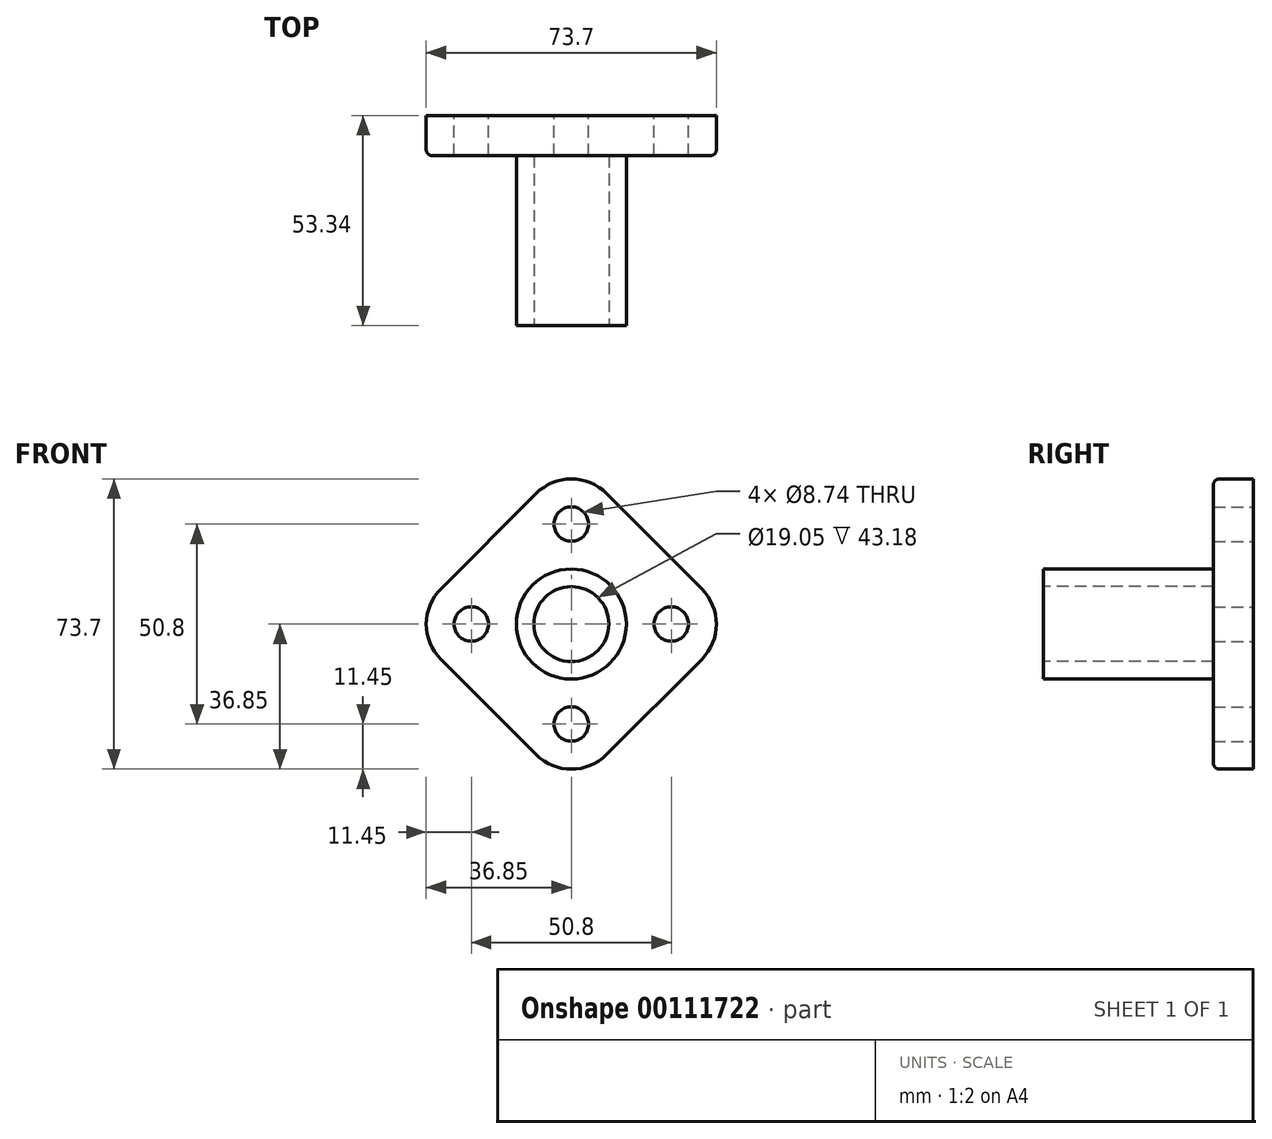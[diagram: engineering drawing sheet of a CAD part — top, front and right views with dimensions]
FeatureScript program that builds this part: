
annotation { "Feature Type Name" : "Feature", "Feature Type Description" : "" }
export const myFeature = defineFeature(function(context is Context, id is Id, definition is map)
    precondition{}
    {
        {
            var Q0;
            Q0=qCreatedBy(makeId("Front.planeOp"),FACE);
            var sketch = newSketch(context, id + "F0", { "sketchPlane" : qUnion([Q0])});
            skLineSegment(sketch, "E0", {"start": v(0, 0) * mm, "end": v(-42.11, 0) * mm});
            skLineSegment(sketch, "E1", {"start": v(0, 0) * mm, "end": v(42.11, 0) * mm});
            skLineSegment(sketch, "E2", {"start": v(0, 0) * mm, "end": v(0, 42.11) * mm});
            skLineSegment(sketch, "E3", {"start": v(0, 0) * mm, "end": v(0, -42.11) * mm});
            skLineSegment(sketch, "E4", {"start": v(0, -42.11) * mm, "end": v(42.11, 0) * mm});
            skLineSegment(sketch, "E5", {"start": v(42.11, 0) * mm, "end": v(0, 42.11) * mm});
            skLineSegment(sketch, "E6", {"start": v(0, 42.11) * mm, "end": v(-42.11, 0) * mm});
            skLineSegment(sketch, "E7", {"start": v(-42.11, 0) * mm, "end": v(0, -42.11) * mm});
            skCircle(sketch, "E8", {"center": v(-25.4, 0) * mm, "radius": 4.37 * mm});
            skCircle(sketch, "E9", {"center": v(25.4, 0) * mm, "radius": 4.37 * mm});
            skCircle(sketch, "E10", {"center": v(0, 25.4) * mm, "radius": 4.37 * mm});
            skCircle(sketch, "E11", {"center": v(0, -25.4) * mm, "radius": 4.37 * mm});
            skSolve(sketch);
        }
        {
            var Q0;
            {var subQ0=sQuery(id+"F0.wireOp",EDGE,"E5");Q0=makeQuery(id+"F0.imprint","IMPRINT",FACE,{"disambiguationData":[TD([[makeQuery(id+"F0.imprint","IMPRINT",EDGE,{"derivedFrom":subQ0}),1.0]])]});}
            var Q1;
            {var subQ0=sQuery(id+"F0.wireOp",EDGE,"E4");Q1=makeQuery(id+"F0.imprint","IMPRINT",FACE,{"disambiguationData":[TD([[makeQuery(id+"F0.imprint","IMPRINT",EDGE,{"derivedFrom":subQ0}),1.0]])]});}
            var Q2;
            {var subQ0=sQuery(id+"F0.wireOp",EDGE,"E7");Q2=makeQuery(id+"F0.imprint","IMPRINT",FACE,{"disambiguationData":[TD([[makeQuery(id+"F0.imprint","IMPRINT",EDGE,{"derivedFrom":subQ0}),1.0]])]});}
            var Q3;
            {var subQ0=sQuery(id+"F0.wireOp",EDGE,"E6");Q3=makeQuery(id+"F0.imprint","IMPRINT",FACE,{"disambiguationData":[TD([[makeQuery(id+"F0.imprint","IMPRINT",EDGE,{"derivedFrom":subQ0}),1.0]])]});}
            extrude(context, id + "F1", {"entities" : qUnion([Q0, Q1, Q2, Q3]), "depth" : 10.16 * mm});
        }
        {
            var Q0;
            Q0=makeQuery(id+"F1.opExtrude","SWEPT_EDGE",EDGE,{"disambiguationData":[OSD([sQuery(id+"F0.wireOp",EDGE,"E2"),sQuery(id+"F0.wireOp",EDGE,"E5"),sQuery(id+"F0.wireOp",EDGE,"E6")])]});
            var Q1;
            Q1=makeQuery(id+"F1.opExtrude","SWEPT_EDGE",EDGE,{"disambiguationData":[OSD([sQuery(id+"F0.wireOp",EDGE,"E0"),sQuery(id+"F0.wireOp",EDGE,"E6"),sQuery(id+"F0.wireOp",EDGE,"E7")])]});
            fillet(context, id + "F2", {"entities" : qUnion([Q0, Q1]), "radius" : 12.7 * mm, "tangentPropagation" : true, "allowEdgeOverflow" : false});
        }
        {
            var Q0;
            Q0=makeQuery(id+"F1.opExtrude","SWEPT_EDGE",EDGE,{"disambiguationData":[OSD([sQuery(id+"F0.wireOp",EDGE,"E1"),sQuery(id+"F0.wireOp",EDGE,"E4"),sQuery(id+"F0.wireOp",EDGE,"E5")])]});
            var Q1;
            Q1=makeQuery(id+"F1.opExtrude","SWEPT_EDGE",EDGE,{"disambiguationData":[OSD([sQuery(id+"F0.wireOp",EDGE,"E3"),sQuery(id+"F0.wireOp",EDGE,"E4"),sQuery(id+"F0.wireOp",EDGE,"E7")])]});
            fillet(context, id + "F3", {"entities" : qUnion([Q0, Q1]), "radius" : 12.7 * mm, "tangentPropagation" : true, "allowEdgeOverflow" : false});
        }
        {
            var Q0;
            Q0=makeQuery(id+"F1.opExtrude","CAP_EDGE",EDGE,{"disambiguationData":[OSD([sQuery(id+"F0.wireOp",EDGE,"E6")])],"isStart":false});
            var Q1;
            {var subQ0=sQuery(id+"F0.wireOp",EDGE,"E6");var subQ1=sQuery(id+"F0.wireOp",EDGE,"E5");Q1=makeQuery(id+"F2.opFillet","BLEND_EDGE",EDGE,{"blendedFrom":[makeQuery(id+"F1.opExtrude","SWEPT_EDGE",EDGE,{"disambiguationData":[OSD([sQuery(id+"F0.wireOp",EDGE,"E2"),subQ1,subQ0])]}),makeQuery(id+"F1.opExtrude","CAP_FACE",FACE,{"disambiguationData":[OSD([sQuery(id+"F0.wireOp",EDGE,"E4"),subQ1,subQ0,sQuery(id+"F0.wireOp",EDGE,"E7"),sQuery(id+"F0.wireOp",EDGE,"E8"),sQuery(id+"F0.wireOp",EDGE,"E9"),sQuery(id+"F0.wireOp",EDGE,"E10"),sQuery(id+"F0.wireOp",EDGE,"E11")])],"isStart":false})],"blendedInto":[makeQuery(id+"F1.opExtrude","CAP_FACE",FACE,{"disambiguationData":[OSD([sQuery(id+"F0.wireOp",EDGE,"E4"),subQ1,subQ0,sQuery(id+"F0.wireOp",EDGE,"E7"),sQuery(id+"F0.wireOp",EDGE,"E8"),sQuery(id+"F0.wireOp",EDGE,"E9"),sQuery(id+"F0.wireOp",EDGE,"E10"),sQuery(id+"F0.wireOp",EDGE,"E11")])],"isStart":false})]});}
            var Q2;
            Q2=makeQuery(id+"F1.opExtrude","CAP_EDGE",EDGE,{"disambiguationData":[OSD([sQuery(id+"F0.wireOp",EDGE,"E5")])],"isStart":false});
            var Q3;
            {var subQ0=sQuery(id+"F0.wireOp",EDGE,"E5");var subQ1=sQuery(id+"F0.wireOp",EDGE,"E4");Q3=makeQuery(id+"F3.opFillet","BLEND_EDGE",EDGE,{"blendedFrom":[makeQuery(id+"F1.opExtrude","SWEPT_EDGE",EDGE,{"disambiguationData":[OSD([sQuery(id+"F0.wireOp",EDGE,"E1"),subQ1,subQ0])]}),makeQuery(id+"F1.opExtrude","CAP_FACE",FACE,{"disambiguationData":[OSD([subQ1,subQ0,sQuery(id+"F0.wireOp",EDGE,"E6"),sQuery(id+"F0.wireOp",EDGE,"E7"),sQuery(id+"F0.wireOp",EDGE,"E8"),sQuery(id+"F0.wireOp",EDGE,"E9"),sQuery(id+"F0.wireOp",EDGE,"E10"),sQuery(id+"F0.wireOp",EDGE,"E11")])],"isStart":false})],"blendedInto":[makeQuery(id+"F1.opExtrude","CAP_FACE",FACE,{"disambiguationData":[OSD([subQ1,subQ0,sQuery(id+"F0.wireOp",EDGE,"E6"),sQuery(id+"F0.wireOp",EDGE,"E7"),sQuery(id+"F0.wireOp",EDGE,"E8"),sQuery(id+"F0.wireOp",EDGE,"E9"),sQuery(id+"F0.wireOp",EDGE,"E10"),sQuery(id+"F0.wireOp",EDGE,"E11")])],"isStart":false})]});}
            var Q4;
            Q4=makeQuery(id+"F1.opExtrude","CAP_EDGE",EDGE,{"disambiguationData":[OSD([sQuery(id+"F0.wireOp",EDGE,"E4")])],"isStart":false});
            var Q5;
            {var subQ0=sQuery(id+"F0.wireOp",EDGE,"E7");var subQ1=sQuery(id+"F0.wireOp",EDGE,"E4");Q5=makeQuery(id+"F3.opFillet","BLEND_EDGE",EDGE,{"blendedFrom":[makeQuery(id+"F1.opExtrude","SWEPT_EDGE",EDGE,{"disambiguationData":[OSD([sQuery(id+"F0.wireOp",EDGE,"E3"),subQ1,subQ0])]}),makeQuery(id+"F1.opExtrude","CAP_FACE",FACE,{"disambiguationData":[OSD([subQ1,sQuery(id+"F0.wireOp",EDGE,"E5"),sQuery(id+"F0.wireOp",EDGE,"E6"),subQ0,sQuery(id+"F0.wireOp",EDGE,"E8"),sQuery(id+"F0.wireOp",EDGE,"E9"),sQuery(id+"F0.wireOp",EDGE,"E10"),sQuery(id+"F0.wireOp",EDGE,"E11")])],"isStart":false})],"blendedInto":[makeQuery(id+"F1.opExtrude","CAP_FACE",FACE,{"disambiguationData":[OSD([subQ1,sQuery(id+"F0.wireOp",EDGE,"E5"),sQuery(id+"F0.wireOp",EDGE,"E6"),subQ0,sQuery(id+"F0.wireOp",EDGE,"E8"),sQuery(id+"F0.wireOp",EDGE,"E9"),sQuery(id+"F0.wireOp",EDGE,"E10"),sQuery(id+"F0.wireOp",EDGE,"E11")])],"isStart":false})]});}
            var Q6;
            Q6=makeQuery(id+"F1.opExtrude","CAP_EDGE",EDGE,{"disambiguationData":[OSD([sQuery(id+"F0.wireOp",EDGE,"E7")])],"isStart":false});
            var Q7;
            {var subQ0=sQuery(id+"F0.wireOp",EDGE,"E7");var subQ1=sQuery(id+"F0.wireOp",EDGE,"E6");Q7=makeQuery(id+"F2.opFillet","BLEND_EDGE",EDGE,{"blendedFrom":[makeQuery(id+"F1.opExtrude","SWEPT_EDGE",EDGE,{"disambiguationData":[OSD([sQuery(id+"F0.wireOp",EDGE,"E0"),subQ1,subQ0])]}),makeQuery(id+"F1.opExtrude","CAP_FACE",FACE,{"disambiguationData":[OSD([sQuery(id+"F0.wireOp",EDGE,"E4"),sQuery(id+"F0.wireOp",EDGE,"E5"),subQ1,subQ0,sQuery(id+"F0.wireOp",EDGE,"E8"),sQuery(id+"F0.wireOp",EDGE,"E9"),sQuery(id+"F0.wireOp",EDGE,"E10"),sQuery(id+"F0.wireOp",EDGE,"E11")])],"isStart":false})],"blendedInto":[makeQuery(id+"F1.opExtrude","CAP_FACE",FACE,{"disambiguationData":[OSD([sQuery(id+"F0.wireOp",EDGE,"E4"),sQuery(id+"F0.wireOp",EDGE,"E5"),subQ1,subQ0,sQuery(id+"F0.wireOp",EDGE,"E8"),sQuery(id+"F0.wireOp",EDGE,"E9"),sQuery(id+"F0.wireOp",EDGE,"E10"),sQuery(id+"F0.wireOp",EDGE,"E11")])],"isStart":false})]});}
            fillet(context, id + "F4", {"entities" : qUnion([Q0, Q1, Q2, Q3, Q4, Q5, Q6, Q7]), "radius" : 1.52 * mm, "tangentPropagation" : true, "allowEdgeOverflow" : false});
        }
        {
            var Q0;
            Q0=makeQuery(id+"F1.opExtrude","CAP_FACE",FACE,{"disambiguationData":[OSD([sQuery(id+"F0.wireOp",EDGE,"E4"),sQuery(id+"F0.wireOp",EDGE,"E5"),sQuery(id+"F0.wireOp",EDGE,"E6"),sQuery(id+"F0.wireOp",EDGE,"E7"),sQuery(id+"F0.wireOp",EDGE,"E8"),sQuery(id+"F0.wireOp",EDGE,"E9"),sQuery(id+"F0.wireOp",EDGE,"E10"),sQuery(id+"F0.wireOp",EDGE,"E11")])],"isStart":false});
            var sketch = newSketch(context, id + "F5", { "sketchPlane" : qUnion([Q0])});
            skCircle(sketch, "E12", {"center": v(0, 0) * mm, "radius": 13.97 * mm});
            skSolve(sketch);
        }
        {
            var Q0;
            Q0=makeQuery(id+"F5.imprint","IMPRINT",FACE,{"disambiguationData":[TD([[makeQuery(id+"F5.imprint","IMPRINT",EDGE,{"derivedFrom":sQuery(id+"F5.wireOp",EDGE,"E12")}),1.0]])]});
            extrude(context, id + "F6", {"entities" : qUnion([Q0]), "operationType" : NewBodyOperationType.ADD, "depth" : 43.18 * mm});
        }
        {
            var Q0;
            Q0=makeQuery(id+"F6.opExtrude","CAP_FACE",FACE,{"disambiguationData":[OSD([sQuery(id+"F5.wireOp",EDGE,"E12")])],"isStart":false});
            var sketch = newSketch(context, id + "F7", { "sketchPlane" : qUnion([Q0])});
            skCircle(sketch, "E13", {"center": v(0, 0) * mm, "radius": 9.53 * mm});
            skLineSegment(sketch, "E14", {"start": v(0, 0) * mm, "end": v(38.1, 0) * mm});
            skLineSegment(sketch, "E15", {"start": v(0, 0) * mm, "end": v(-38.1, 0) * mm});
            skLineSegment(sketch, "E16", {"start": v(0, 0) * mm, "end": v(0, 38.1) * mm});
            skLineSegment(sketch, "E17", {"start": v(0, 0) * mm, "end": v(0, -38.1) * mm});
            skPoint(sketch, "E18", {"position": v(-44.45, -38.1) * mm});
            skLineSegment(sketch, "E19.bottom", {"start": v(-44.45, -38.1) * mm, "end": v(-25.4, -38.1) * mm});
            skLineSegment(sketch, "E19.top", {"start": v(-44.45, -19.05) * mm, "end": v(-25.4, -19.05) * mm});
            skLineSegment(sketch, "E19.left", {"start": v(-44.45, -38.1) * mm, "end": v(-44.45, -19.05) * mm});
            skLineSegment(sketch, "E19.right", {"start": v(-25.4, -38.1) * mm, "end": v(-25.4, -19.05) * mm});
            skCircle(sketch, "E20", {"center": v(-25.4, -19.05) * mm, "radius": 5.16 * mm});
            skLineSegment(sketch, "E21.bottom", {"start": v(44.45, -38.1) * mm, "end": v(25.4, -38.1) * mm});
            skLineSegment(sketch, "E21.top", {"start": v(44.45, -19.05) * mm, "end": v(25.4, -19.05) * mm});
            skLineSegment(sketch, "E21.left", {"start": v(44.45, -38.1) * mm, "end": v(44.45, -19.05) * mm});
            skLineSegment(sketch, "E21.right", {"start": v(25.4, -38.1) * mm, "end": v(25.4, -19.05) * mm});
            skLineSegment(sketch, "E22.bottom", {"start": v(-44.45, 50.8) * mm, "end": v(-25.4, 50.8) * mm});
            skLineSegment(sketch, "E22.top", {"start": v(-44.45, 31.75) * mm, "end": v(-25.4, 31.75) * mm});
            skLineSegment(sketch, "E22.left", {"start": v(-44.45, 50.8) * mm, "end": v(-44.45, 31.75) * mm});
            skLineSegment(sketch, "E22.right", {"start": v(-25.4, 50.8) * mm, "end": v(-25.4, 31.75) * mm});
            skLineSegment(sketch, "E23.bottom", {"start": v(44.45, 50.8) * mm, "end": v(25.4, 50.8) * mm});
            skLineSegment(sketch, "E23.top", {"start": v(44.45, 31.75) * mm, "end": v(25.4, 31.75) * mm});
            skLineSegment(sketch, "E23.left", {"start": v(44.45, 50.8) * mm, "end": v(44.45, 31.75) * mm});
            skLineSegment(sketch, "E23.right", {"start": v(25.4, 50.8) * mm, "end": v(25.4, 31.75) * mm});
            skCircle(sketch, "E24", {"center": v(-25.4, 31.75) * mm, "radius": 5.16 * mm});
            skCircle(sketch, "E25", {"center": v(25.4, 31.75) * mm, "radius": 5.16 * mm});
            skCircle(sketch, "E26", {"center": v(25.4, -19.05) * mm, "radius": 5.16 * mm});
            skArc(sketch, "E27", {"start": v(25.4, -38.1) * mm, "mid": v(0, -28.4) * mm, "end": v(-25.4, -38.1) * mm});
            skArc(sketch, "E28", {"start": v(-44.45, -19.05) * mm, "mid": v(-34.75, 6.35) * mm, "end": v(-44.45, 31.75) * mm});
            skArc(sketch, "E29", {"start": v(44.45, 31.75) * mm, "mid": v(34.75, 6.35) * mm, "end": v(44.45, -19.05) * mm});
            skArc(sketch, "E30", {"start": v(-25.4, 50.8) * mm, "mid": v(0, 41.1) * mm, "end": v(25.4, 50.8) * mm});
            skSolve(sketch);
        }
        {
            var Q0;
            Q0=makeQuery(id+"F7.imprint","IMPRINT",FACE,{"disambiguationData":[TD([[makeQuery(id+"F7.imprint","IMPRINT",EDGE,{"derivedFrom":sQuery(id+"F7.wireOp",EDGE,"E13")}),1.0]])]});
            extrude(context, id + "F8", {"entities" : qUnion([Q0]), "operationType" : NewBodyOperationType.REMOVE, "oppositeDirection" : true, "depth" : 43.18 * mm});
        }
    });
